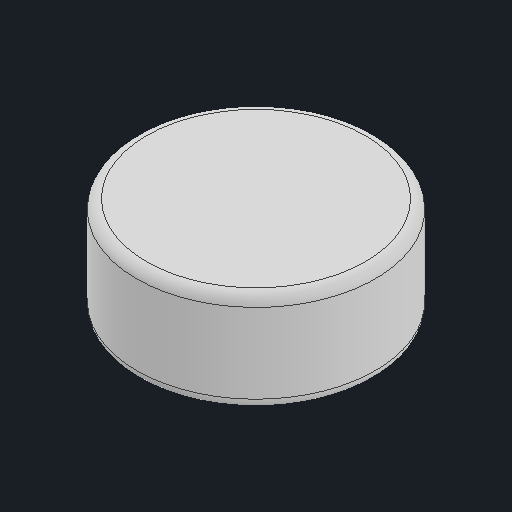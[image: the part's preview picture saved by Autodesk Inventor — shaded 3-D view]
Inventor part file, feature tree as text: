
AUTODESK INVENTOR PART (.ipt)
format: ipt  version: 2024 (Build 280153000, 153)  size: 97,280 bytes
history: native  units: in
note: dims shown in document units (in); Inventor stores cm internally (conversion verified against a paired STEP export)
features: fillet x1
ambient origin geometry x8: Origin, YZ Plane, XZ Plane, XY Plane, X Axis, Y Axis, Z Axis, Center Point
bodies: Solid1 (feature_tree)
feature tree (1):
  fillet  "Fillet1"  [1 undecoded]
note: 1 required parameter value undecoded (feature->parameter linkage not recoverable at this tier; creation-order binding heuristic only, values carry confidence <= 0.55)
